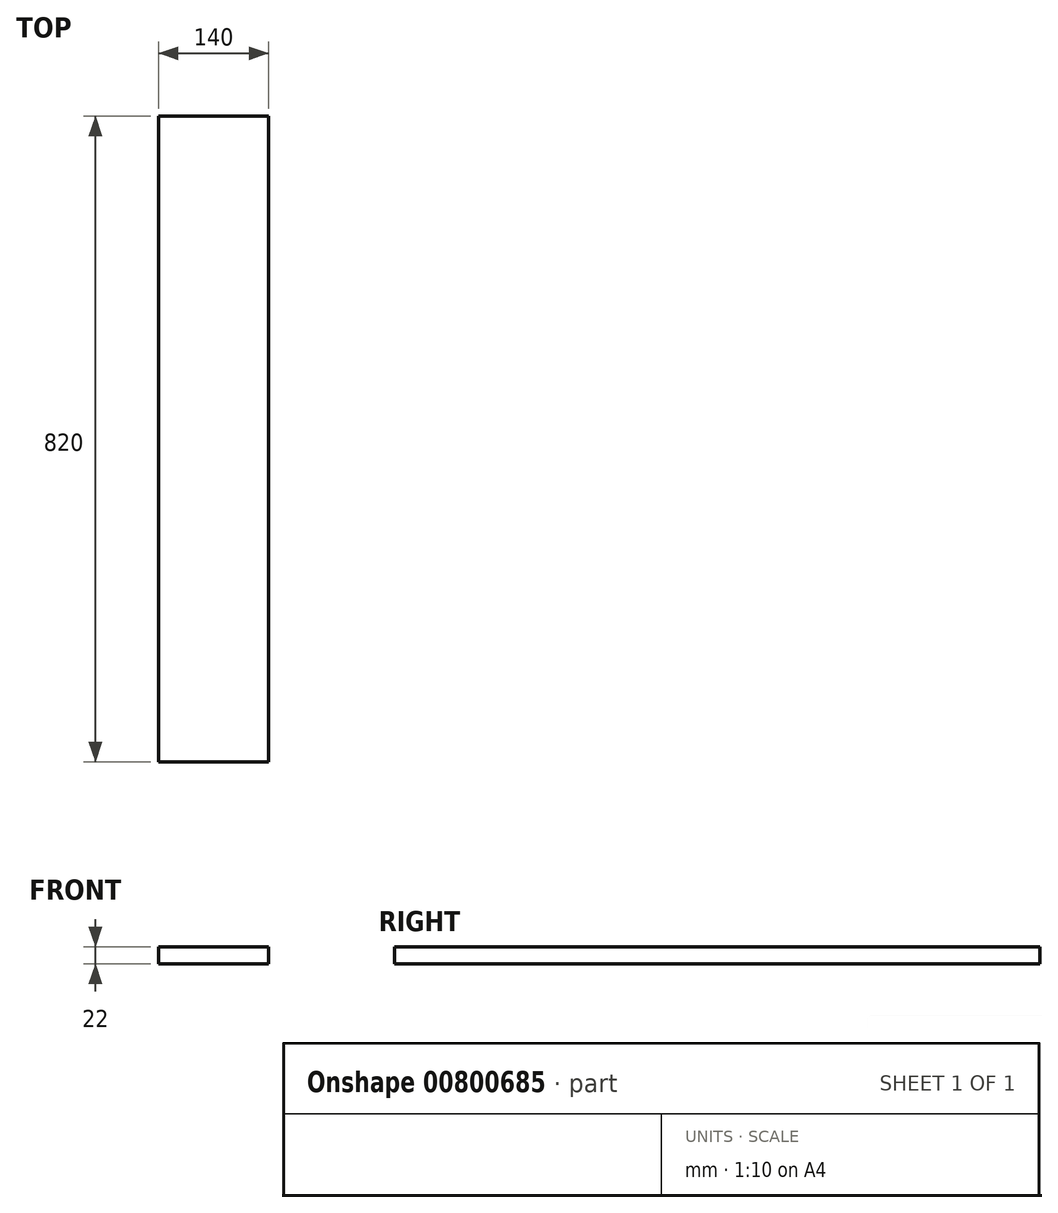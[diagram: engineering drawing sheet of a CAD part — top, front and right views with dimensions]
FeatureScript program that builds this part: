
annotation { "Feature Type Name" : "Feature", "Feature Type Description" : "" }
export const myFeature = defineFeature(function(context is Context, id is Id, definition is map)
    precondition{}
    {
        {
            var Q0;
            Q0=qCreatedBy(makeId("Top.planeOp"),FACE);
            var sketch = newSketch(context, id + "F0", { "sketchPlane" : qUnion([Q0])});
            skLineSegment(sketch, "E0.bottom", {"start": v(70, 410) * mm, "end": v(-70, 410) * mm});
            skLineSegment(sketch, "E0.top", {"start": v(70, -410) * mm, "end": v(-70, -410) * mm});
            skLineSegment(sketch, "E0.left", {"start": v(70, 410) * mm, "end": v(70, -410) * mm});
            skLineSegment(sketch, "E0.right", {"start": v(-70, 410) * mm, "end": v(-70, -410) * mm});
            skPoint(sketch, "E0.middle", {"position": v(0, 0) * mm});
            skSolve(sketch);
        }
        {
            var Q0;
            Q0 = qSketchRegion(id + "F0", true);
            extrude(context, id + "F1", {"entities" : qUnion([Q0]), "depth" : 22 * mm, "offsetDistance" : 25 * mm});
        }
    });
